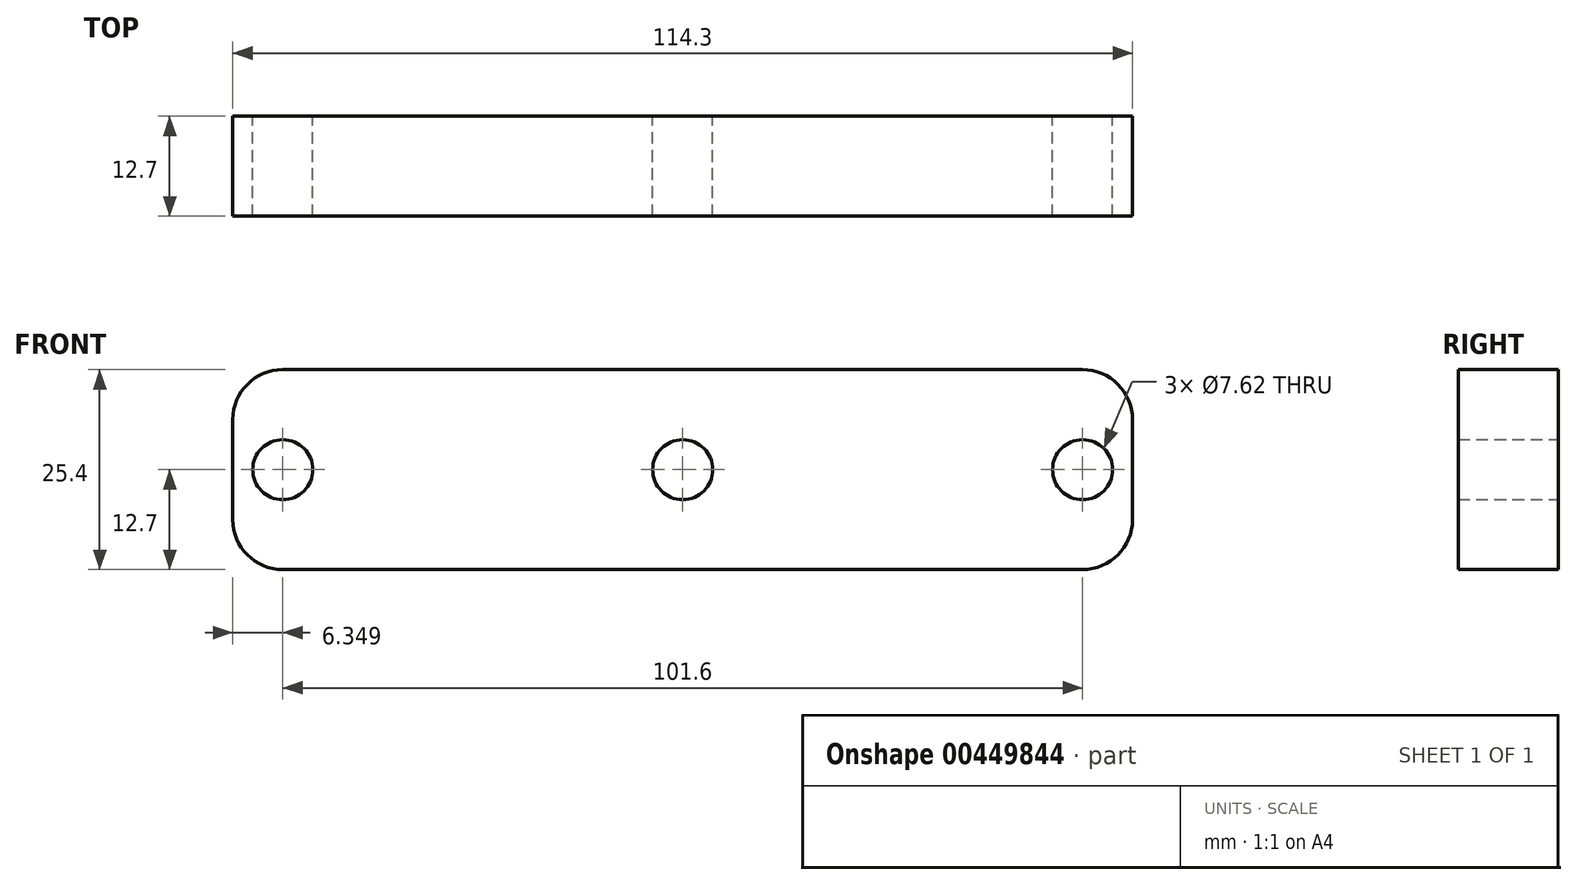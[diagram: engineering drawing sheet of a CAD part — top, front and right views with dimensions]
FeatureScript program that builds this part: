
annotation { "Feature Type Name" : "Feature", "Feature Type Description" : "" }
export const myFeature = defineFeature(function(context is Context, id is Id, definition is map)
    precondition{}
    {
        {
            var Q0;
            Q0=qCreatedBy(makeId("Front.planeOp"),FACE);
            var sketch = newSketch(context, id + "F0", { "sketchPlane" : qUnion([Q0])});
            skLineSegment(sketch, "E0.bottom", {"start": v(-60.04, 7.12) * mm, "end": v(41.56, 7.12) * mm});
            skLineSegment(sketch, "E0.top", {"start": v(-60.04, -18.28) * mm, "end": v(41.56, -18.28) * mm});
            skLineSegment(sketch, "E0.left", {"start": v(-66.4, 0.77) * mm, "end": v(-66.4, -11.93) * mm});
            skLineSegment(sketch, "E0.right", {"start": v(47.9, 0.77) * mm, "end": v(47.9, -11.93) * mm});
            skPoint(sketch, "E1.visualSharp", {"position": v(-66.4, 7.12) * mm});
            skArc(sketch, "E1.filletArc", {"start": v(-60.04, 7.12) * mm, "mid": v(-64.53, 5.26) * mm, "end": v(-66.4, 0.77) * mm});
            skPoint(sketch, "E2.visualSharp", {"position": v(-66.4, -18.28) * mm});
            skArc(sketch, "E2.filletArc", {"start": v(-66.4, -11.93) * mm, "mid": v(-64.53, -16.42) * mm, "end": v(-60.04, -18.28) * mm});
            skPoint(sketch, "E3.visualSharp", {"position": v(47.9, -18.28) * mm});
            skArc(sketch, "E3.filletArc", {"start": v(41.56, -18.28) * mm, "mid": v(46.05, -16.42) * mm, "end": v(47.9, -11.93) * mm});
            skPoint(sketch, "E4.visualSharp", {"position": v(47.9, 7.12) * mm});
            skArc(sketch, "E4.filletArc", {"start": v(47.9, 0.77) * mm, "mid": v(46.05, 5.26) * mm, "end": v(41.56, 7.12) * mm});
            skCircle(sketch, "E5", {"center": v(-60.04, -5.58) * mm, "radius": 3.81 * mm});
            skPoint(sketch, "E5.centerSnap0", {"position": v(-66.4, -5.58) * mm});
            skCircle(sketch, "E6", {"center": v(41.56, -5.58) * mm, "radius": 3.81 * mm});
            skCircle(sketch, "E7", {"center": v(-9.24, -5.58) * mm, "radius": 3.81 * mm});
            skPoint(sketch, "E7.centerSnap0", {"position": v(-9.24, 7.12) * mm});
            skSolve(sketch);
        }
        {
            var Q0;
            Q0=makeQuery(id+"F0.imprint","IMPRINT",FACE,{"disambiguationData":[TD([[makeQuery(id+"F0.imprint","IMPRINT",EDGE,{"derivedFrom":sQuery(id+"F0.wireOp",EDGE,"E0.bottom")}),-1.0]])]});
            extrude(context, id + "F1", {"entities" : qUnion([Q0]), "depth" : 12.7 * mm});
        }
    });
